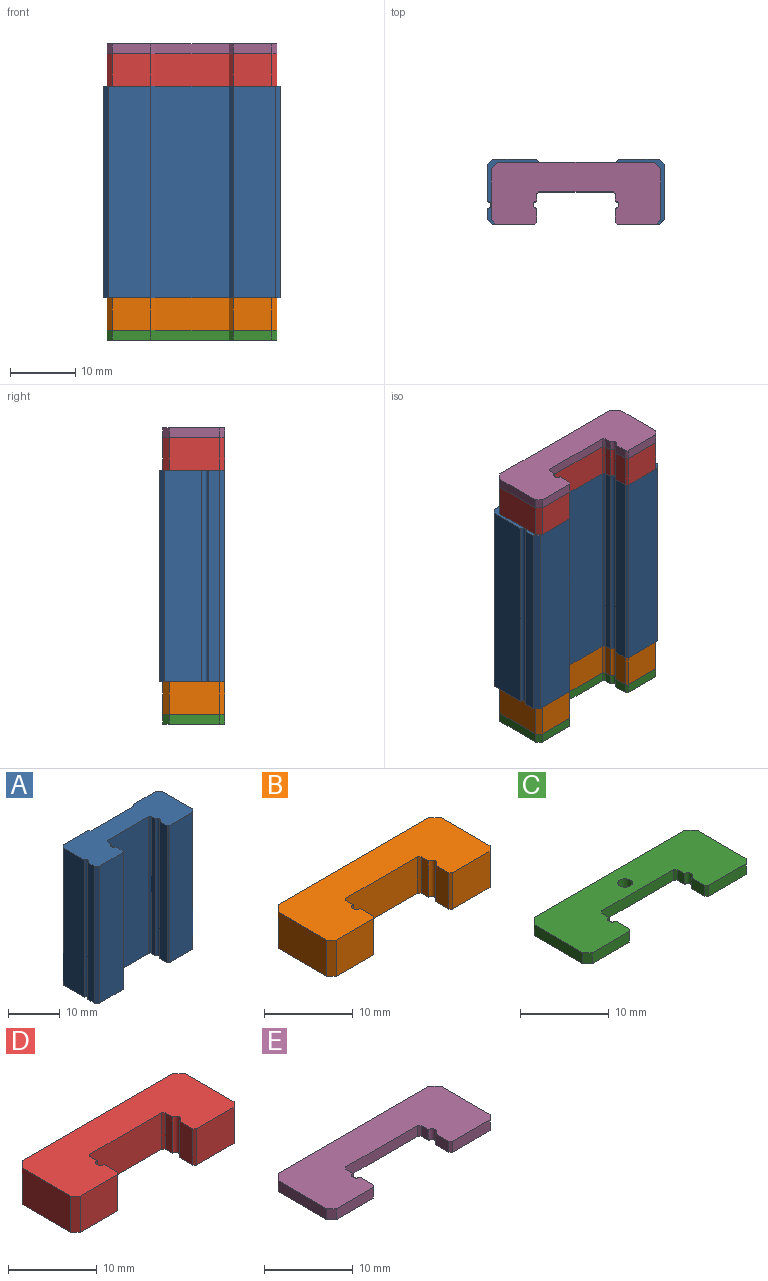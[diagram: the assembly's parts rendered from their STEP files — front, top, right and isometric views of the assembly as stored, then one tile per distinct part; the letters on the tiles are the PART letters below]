
ASSEMBLY  parts=5 mates=13
PART A: 36 faces, bbox 27x10x32.4 mm
  f0: plane 32.4x5.75mm, normal (-1,0,0), area 186.3mm2, adj f7,f8,f27,f31
  f1: plane 32.4x6.45mm, normal (0,-1,0), area 209mm2, adj f7,f8,f29,f32
  f2: plane 32.4x6.25mm, normal (0,1,0), area 192.7mm2, adj f7,f8,f10,f14,f19,f30
  f3: plane 32.4x6.7mm, normal (0,1,0), area 207.3mm2, adj f7,f8,f12,f16,f18,f31
  f4: plane 32.4x8.5mm, normal (1,0,0), area 275.4mm2, adj f7,f8,f28,f30
  f5: plane 32.4x1.75mm, normal (-1,0,0), area 56.7mm2, adj f7,f8,f27,f29
  f6: plane 32.4x6.45mm, normal (0,-1,0), area 209mm2, adj f7,f8,f28,f33
  f7: plane 27x10mm, normal (0,0,1), area 201.5mm2, adj f0,f1,f2,f3,f4,f5,f6,f17
  f8: plane 27x10mm, normal (0,0,-1), area 201.5mm2, adj f0,f1,f2,f3,f4,f5,f6,f17
  f9: cone r=1.25mm half-angle=59deg, axis (0,1,0), area 5.7mm2, adj f10
  f10: cylinder r=1.25mm len=7.5mm, axis (0,1,0), area 58.9mm2, adj f2,f9
  f11: cone r=1.25mm half-angle=59deg, axis (0,1,0), area 5.7mm2, adj f12
  f12: cylinder r=1.25mm len=7.5mm, axis (0,1,0), area 58.9mm2, adj f3,f11
  f13: cone r=1.25mm half-angle=59deg, axis (0,1,0), area 5.7mm2, adj f14
  f14: cylinder r=1.25mm len=7.5mm, axis (0,1,0), area 58.9mm2, adj f2,f13
  f15: cone r=1.25mm half-angle=59deg, axis (0,1,0), area 5.7mm2, adj f16
  f16: cylinder r=1.25mm len=7.5mm, axis (0,1,0), area 58.9mm2, adj f3,f15
  f17: plane 32.4x11.55mm, normal (0,1,0), area 374.2mm2, adj f7,f8,f18,f19
  f18: plane 32.4x0.5mm, normal (0.71,0.71,0), area 22.9mm2, adj f3,f7,f8,f17
  f19: plane 32.4x0.5mm, normal (-0.71,0.71,0), area 22.9mm2, adj f2,f7,f8,f17
  f20: plane 32.4x1.14mm, normal (1,0,0), area 37mm2, adj f7,f8,f21,f35
  f21: cylinder r=0.56mm len=32.4mm, axis (0,0,-1), area 56.9mm2, adj f7,f8,f20,f22
  f22: plane 32.4x2.14mm, normal (1,0,0), area 69.4mm2, adj f7,f8,f21,f32
  f23: plane 32.4x2.14mm, normal (-1,0,0), area 69.4mm2, adj f7,f8,f24,f33
  f24: cylinder r=0.56mm len=32.4mm, axis (0,0,-1), area 56.9mm2, adj f7,f8,f23,f25
  f25: plane 32.4x1.14mm, normal (-1,0,0), area 37mm2, adj f7,f8,f24,f34
  f26: plane 32.4x11.4mm, normal (0,-1,0), area 369.4mm2, adj f7,f8,f34,f35
  f27: cylinder r=0.5mm len=32.4mm, axis (0,0,1), area 50.9mm2, adj f0,f5,f7,f8
  f28: plane 32.4x0.75mm, normal (0.71,-0.71,0), area 34.4mm2, adj f4,f6,f7,f8
  f29: plane 32.4x0.75mm, normal (-0.71,-0.71,0), area 34.4mm2, adj f1,f5,f7,f8
  f30: plane 32.4x0.75mm, normal (0.71,0.71,0), area 34.4mm2, adj f2,f4,f7,f8
  f31: plane 32.4x0.75mm, normal (-0.71,0.71,0), area 34.4mm2, adj f0,f3,f7,f8
  f32: plane 32.4x0.3mm, normal (0.71,-0.71,0), area 13.7mm2, adj f1,f7,f8,f22
  f33: plane 32.4x0.3mm, normal (-0.71,-0.71,0), area 13.7mm2, adj f6,f7,f8,f23
  f34: plane 32.4x0.3mm, normal (-0.71,-0.71,0), area 13.7mm2, adj f7,f8,f25,f26
  f35: plane 32.4x0.3mm, normal (0.71,-0.71,0), area 13.7mm2, adj f7,f8,f20,f26
PART B: 24 faces, bbox 26x9.5x5 mm
  f0: plane 7.75x5mm, normal (-1,0,0), area 38.8mm2, adj f12,f13,f15,f17
  f1: plane 24x5mm, normal (0,1,0), area 120mm2, adj f12,f13,f14,f15
  f2: plane 7.75x5mm, normal (1,0,0), area 38.8mm2, adj f12,f13,f14,f16
  f3: plane 5.95x5mm, normal (0,-1,0), area 29.8mm2, adj f12,f13,f16,f18
  f4: plane 5x2.14mm, normal (-1,0,0), area 10.7mm2, adj f5,f12,f13,f18
  f5: cylinder r=0.56mm len=5mm, axis (0,0,1), area 8.8mm2, adj f4,f6,f12,f13
  f6: plane 5x1.14mm, normal (-1,0,0), area 5.7mm2, adj f5,f12,f13,f19
  f7: plane 11.4x5mm, normal (0,-1,0), area 57mm2, adj f12,f13,f19,f21
  f8: plane 5x1.14mm, normal (1,0,0), area 5.7mm2, adj f9,f12,f13,f21
  f9: cylinder r=0.56mm len=5mm, axis (0,0,1), area 8.8mm2, adj f8,f10,f12,f13
  f10: plane 5x2.14mm, normal (1,0,0), area 10.7mm2, adj f9,f12,f13,f20
  f11: plane 5.95x5mm, normal (0,-1,0), area 29.8mm2, adj f12,f13,f17,f20
  f12: plane 26x9.5mm, normal (0,0,-1), area 182.4mm2, adj f0,f1,f2,f3,f4,f5,f6,f7
  f13: plane 26x9.5mm, normal (0,0,1), area 184.5mm2, adj f0,f1,f2,f3,f4,f5,f6,f7
  f14: plane 5x1mm, normal (0.71,0.71,0), area 7.1mm2, adj f1,f2,f12,f13
  f15: plane 5x1mm, normal (-0.71,0.71,0), area 7.1mm2, adj f0,f1,f12,f13
  f16: plane 5x0.75mm, normal (0.71,-0.71,0), area 5.3mm2, adj f2,f3,f12,f13
  f17: plane 5x0.75mm, normal (-0.71,-0.71,0), area 5.3mm2, adj f0,f11,f12,f13
  f18: plane 5x0.3mm, normal (-0.71,-0.71,0), area 2.1mm2, adj f3,f4,f12,f13
  f19: plane 5x0.3mm, normal (-0.71,-0.71,0), area 2.1mm2, adj f6,f7,f12,f13
  f20: plane 5x0.3mm, normal (0.71,-0.71,0), area 2.1mm2, adj f10,f11,f12,f13
  f21: plane 5x0.3mm, normal (0.71,-0.71,0), area 2.1mm2, adj f7,f8,f12,f13
  f22: cylinder r=0.81mm len=1.63mm, axis (0,0,-1), area 5.1mm2, adj f12,f23
  f23: plane 1.63x1.63mm, normal (0,0,-1), area 2.1mm2, adj f22
PART C: 23 faces, bbox 26x9.5x1.5 mm
  f0: plane 5.95x1.5mm, normal (0,-1,0), area 8.9mm2, adj f12,f13,f16,f21
  f1: plane 7.75x1.5mm, normal (-1,0,0), area 11.6mm2, adj f12,f13,f15,f16
  f2: plane 24x1.5mm, normal (0,1,0), area 36mm2, adj f12,f13,f14,f15
  f3: plane 7.75x1.5mm, normal (1,0,0), area 11.6mm2, adj f12,f13,f14,f17
  f4: plane 5.95x1.5mm, normal (0,-1,0), area 8.9mm2, adj f12,f13,f17,f20
  f5: plane 2.14x1.5mm, normal (-1,0,0), area 3.2mm2, adj f6,f12,f13,f20
  f6: cylinder r=0.56mm len=1.5mm, axis (0,0,1), area 2.6mm2, adj f5,f7,f12,f13
  f7: plane 1.5x1.14mm, normal (-1,0,0), area 1.7mm2, adj f6,f12,f13,f19
  f8: plane 11.4x1.5mm, normal (0,-1,0), area 17.1mm2, adj f12,f13,f18,f19
  f9: plane 1.5x1.14mm, normal (1,0,0), area 1.7mm2, adj f10,f12,f13,f18
  f10: cylinder r=0.56mm len=1.5mm, axis (0,0,1), area 2.6mm2, adj f9,f11,f12,f13
  f11: plane 2.14x1.5mm, normal (1,0,0), area 3.2mm2, adj f10,f12,f13,f21
  f12: plane 26x9.5mm, normal (0,0,-1), area 182.4mm2, adj f0,f1,f2,f3,f4,f5,f6,f7
  f13: plane 26x9.5mm, normal (0,0,1), area 182.4mm2, adj f0,f1,f2,f3,f4,f5,f6,f7
  f14: plane 1.5x1mm, normal (0.71,0.71,0), area 2.1mm2, adj f2,f3,f12,f13
  f15: plane 1.5x1mm, normal (-0.71,0.71,0), area 2.1mm2, adj f1,f2,f12,f13
  f16: plane 1.5x0.75mm, normal (-0.71,-0.71,0), area 1.6mm2, adj f0,f1,f12,f13
  f17: plane 1.5x0.75mm, normal (0.71,-0.71,0), area 1.6mm2, adj f3,f4,f12,f13
  f18: plane 1.5x0.3mm, normal (0.71,-0.71,0), area 0.6mm2, adj f8,f9,f12,f13
  f19: plane 1.5x0.3mm, normal (-0.71,-0.71,0), area 0.6mm2, adj f7,f8,f12,f13
  f20: plane 1.5x0.3mm, normal (-0.71,-0.71,0), area 0.6mm2, adj f4,f5,f12,f13
  f21: plane 1.5x0.3mm, normal (0.71,-0.71,0), area 0.6mm2, adj f0,f11,f12,f13
  f22: cylinder r=0.81mm len=1.63mm, axis (0,0,-1), area 7.7mm2, adj f12,f13
PART D: 22 faces, bbox 26x9.5x5 mm
  f0: plane 7.75x5mm, normal (-1,0,0), area 38.8mm2, adj f12,f13,f15,f17
  f1: plane 24x5mm, normal (0,1,0), area 120mm2, adj f12,f13,f14,f15
  f2: plane 7.75x5mm, normal (1,0,0), area 38.8mm2, adj f12,f13,f14,f16
  f3: plane 5.95x5mm, normal (0,-1,0), area 29.8mm2, adj f12,f13,f16,f18
  f4: plane 5x2.14mm, normal (-1,0,0), area 10.7mm2, adj f5,f12,f13,f18
  f5: cylinder r=0.56mm len=5mm, axis (0,0,-1), area 8.8mm2, adj f4,f6,f12,f13
  f6: plane 5x1.14mm, normal (-1,0,0), area 5.7mm2, adj f5,f12,f13,f21
  f7: plane 11.4x5mm, normal (0,-1,0), area 57mm2, adj f12,f13,f20,f21
  f8: plane 5x1.14mm, normal (1,0,0), area 5.7mm2, adj f9,f12,f13,f20
  f9: cylinder r=0.56mm len=5mm, axis (0,0,-1), area 8.8mm2, adj f8,f10,f12,f13
  f10: plane 5x2.14mm, normal (1,0,0), area 10.7mm2, adj f9,f12,f13,f19
  f11: plane 5.95x5mm, normal (0,-1,0), area 29.8mm2, adj f12,f13,f17,f19
  f12: plane 26x9.5mm, normal (0,0,1), area 184.5mm2, adj f0,f1,f2,f3,f4,f5,f6,f7
  f13: plane 26x9.5mm, normal (0,0,-1), area 184.5mm2, adj f0,f1,f2,f3,f4,f5,f6,f7
  f14: plane 5x1mm, normal (0.71,0.71,0), area 7.1mm2, adj f1,f2,f12,f13
  f15: plane 5x1mm, normal (-0.71,0.71,0), area 7.1mm2, adj f0,f1,f12,f13
  f16: plane 5x0.75mm, normal (0.71,-0.71,0), area 5.3mm2, adj f2,f3,f12,f13
  f17: plane 5x0.75mm, normal (-0.71,-0.71,0), area 5.3mm2, adj f0,f11,f12,f13
  f18: plane 5x0.3mm, normal (-0.71,-0.71,0), area 2.1mm2, adj f3,f4,f12,f13
  f19: plane 5x0.3mm, normal (0.71,-0.71,0), area 2.1mm2, adj f10,f11,f12,f13
  f20: plane 5x0.3mm, normal (0.71,-0.71,0), area 2.1mm2, adj f7,f8,f12,f13
  f21: plane 5x0.3mm, normal (-0.71,-0.71,0), area 2.1mm2, adj f6,f7,f12,f13
PART E: 22 faces, bbox 26x9.5x1.5 mm
  f0: plane 5.95x1.5mm, normal (0,-1,0), area 8.9mm2, adj f12,f13,f16,f21
  f1: plane 7.75x1.5mm, normal (-1,0,0), area 11.6mm2, adj f12,f13,f15,f16
  f2: plane 24x1.5mm, normal (0,1,0), area 36mm2, adj f12,f13,f14,f15
  f3: plane 7.75x1.5mm, normal (1,0,0), area 11.6mm2, adj f12,f13,f14,f17
  f4: plane 5.95x1.5mm, normal (0,-1,0), area 8.9mm2, adj f12,f13,f17,f20
  f5: plane 2.14x1.5mm, normal (-1,0,0), area 3.2mm2, adj f6,f12,f13,f20
  f6: cylinder r=0.56mm len=1.5mm, axis (0,0,-1), area 2.6mm2, adj f5,f7,f12,f13
  f7: plane 1.5x1.14mm, normal (-1,0,0), area 1.7mm2, adj f6,f12,f13,f18
  f8: plane 11.4x1.5mm, normal (0,-1,0), area 17.1mm2, adj f12,f13,f18,f19
  f9: plane 1.5x1.14mm, normal (1,0,0), area 1.7mm2, adj f10,f12,f13,f19
  f10: cylinder r=0.56mm len=1.5mm, axis (0,0,-1), area 2.6mm2, adj f9,f11,f12,f13
  f11: plane 2.14x1.5mm, normal (1,0,0), area 3.2mm2, adj f10,f12,f13,f21
  f12: plane 26x9.5mm, normal (0,0,1), area 184.5mm2, adj f0,f1,f2,f3,f4,f5,f6,f7
  f13: plane 26x9.5mm, normal (0,0,-1), area 184.5mm2, adj f0,f1,f2,f3,f4,f5,f6,f7
  f14: plane 1.5x1mm, normal (0.71,0.71,0), area 2.1mm2, adj f2,f3,f12,f13
  f15: plane 1.5x1mm, normal (-0.71,0.71,0), area 2.1mm2, adj f1,f2,f12,f13
  f16: plane 1.5x0.75mm, normal (-0.71,-0.71,0), area 1.6mm2, adj f0,f1,f12,f13
  f17: plane 1.5x0.75mm, normal (0.71,-0.71,0), area 1.6mm2, adj f3,f4,f12,f13
  f18: plane 1.5x0.3mm, normal (-0.71,-0.71,0), area 0.6mm2, adj f7,f8,f12,f13
  f19: plane 1.5x0.3mm, normal (0.71,-0.71,0), area 0.6mm2, adj f8,f9,f12,f13
  f20: plane 1.5x0.3mm, normal (-0.71,-0.71,0), area 0.6mm2, adj f4,f5,f12,f13
  f21: plane 1.5x0.3mm, normal (0.71,-0.71,0), area 0.6mm2, adj f0,f11,f12,f13
PLACE A t=(0,-10,6.5)mm
PLACE B t=(0,-10,6.5)mm
PLACE C t=(0,-10,6.5)mm
PLACE D t=(0,-10,6.5)mm
PLACE E t=(0,-10,6.5)mm
MATE planar A.f1 <-> B.f11  axis (0,-1,0) through (-9.53,-7,22.7)mm
MATE planar D.f11 <-> A.f1  axis (0,-1,0) through (-9.28,-7,41.4)mm
MATE planar B.f12 <-> C.f13  axis (0,0,-1) through (12.25,-7,1.5)mm
MATE planar B.f11 <-> C.f0  axis (0,-1,0) through (-9.28,-7,4)mm
MATE planar E.f13 <-> D.f12  axis (0,0,-1) through (0,-1.52,43.9)mm
MATE planar D.f4 <-> E.f5  axis (-1,0,0) through (6,-5.63,41.4)mm
MATE planar E.f2 <-> D.f1  axis (0,1,0) through (0,2.5,45.4)mm
MATE planar C.f1 <-> B.f0  axis (-1,0,0) through (-13,-2.37,0.75)mm
MATE planar A.f8 <-> B.f13  axis (0,0,-1) through (-13.5,-0.62,6.5)mm
MATE planar D.f13 <-> A.f7  axis (0,0,-1) through (0,-1.52,38.9)mm
MATE planar A.f23 <-> B.f4  axis (-1,0,0) through (6,-5.63,22.7)mm
MATE planar A.f1 <-> C.f0  axis (0,-1,0) through (-9.53,-7,22.7)mm
MATE planar A.f23 <-> D.f4  axis (-1,0,0) through (6,-5.63,38.9)mm
